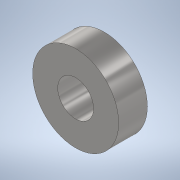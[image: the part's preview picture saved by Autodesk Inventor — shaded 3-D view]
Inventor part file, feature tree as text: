
AUTODESK INVENTOR PART (.ipt)
format: ipt  version: 2022 (Build 260153000, 153)  size: 102,912 bytes
history: native  units: in
note: dims shown in document units (in); Inventor stores cm internally (conversion verified against a paired STEP export)
features: extrude x1, sketch x1
ambient origin geometry x8: Origin, YZ Plane, XZ Plane, XY Plane, X Axis, Y Axis, Z Axis, Center Point
bodies: Solid1 (feature_tree)
feature tree (2):
  extrude  "Extrusion1"  Depth=0.3937in
  sketch  "Sketch1"  dims[d0=0.9449in d1=0.3937in d2=0.315in d3=0.0in]
